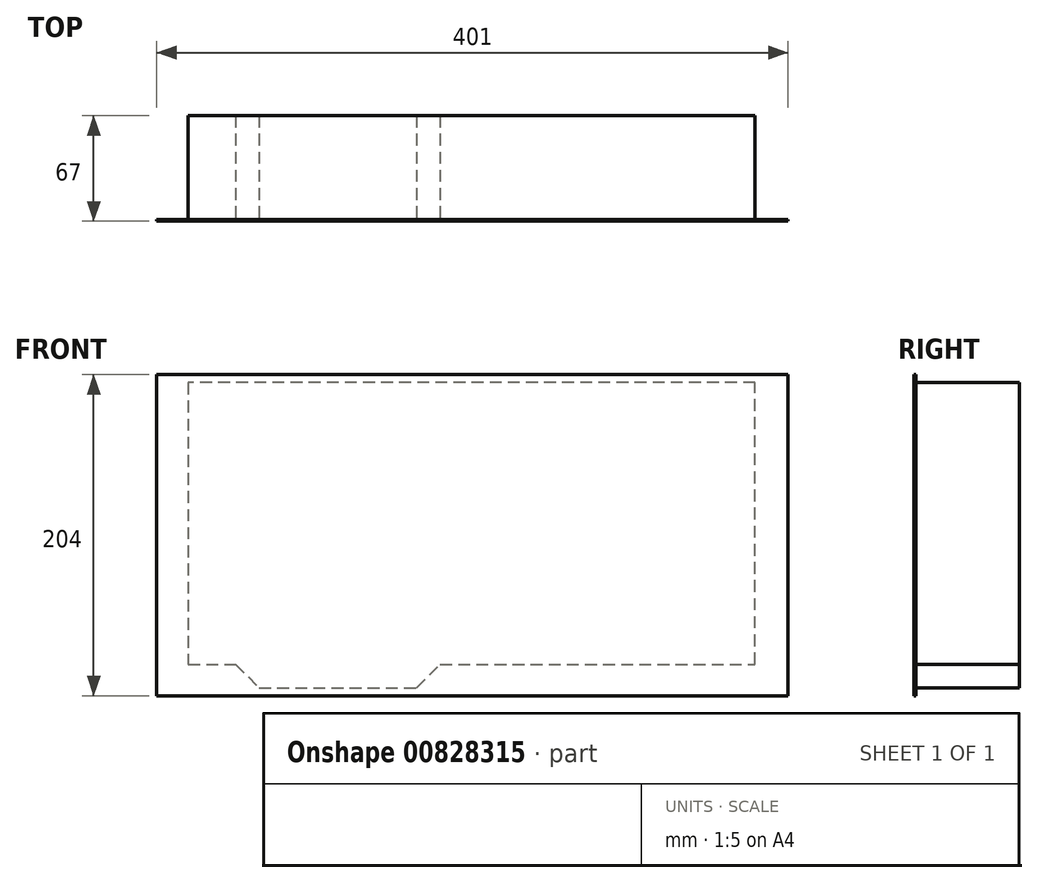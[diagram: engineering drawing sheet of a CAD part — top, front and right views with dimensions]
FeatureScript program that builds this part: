
annotation { "Feature Type Name" : "Feature", "Feature Type Description" : "" }
export const myFeature = defineFeature(function(context is Context, id is Id, definition is map)
    precondition{}
    {
        {
            var Q0;
            Q0=qCreatedBy(makeId("Front.planeOp"),FACE);
            var sketch = newSketch(context, id + "F0", { "sketchPlane" : qUnion([Q0])});
            skLineSegment(sketch, "E0.bottom", {"start": v(0, 0) * mm, "end": v(401, 0) * mm});
            skLineSegment(sketch, "E0.top", {"start": v(0, 204) * mm, "end": v(401, 204) * mm});
            skLineSegment(sketch, "E0.left", {"start": v(0, 0) * mm, "end": v(0, 204) * mm});
            skLineSegment(sketch, "E0.right", {"start": v(401, 0) * mm, "end": v(401, 204) * mm});
            skSolve(sketch);
        }
        {
            var Q0;
            Q0=makeQuery(id+"F0.imprint","IMPRINT",FACE,{"disambiguationData":[TD([[makeQuery(id+"F0.imprint","IMPRINT",EDGE,{"derivedFrom":sQuery(id+"F0.wireOp",EDGE,"E0.bottom")}),1.0]])]});
            extrude(context, id + "F1", {"entities" : qUnion([Q0]), "depth" : 1 * mm, "offsetDistance" : 25 * mm});
        }
        {
            var Q0;
            Q0=makeQuery(id+"F1.opExtrude","CAP_FACE",FACE,{"disambiguationData":[OSD([sQuery(id+"F0.wireOp",EDGE,"E0.bottom"),sQuery(id+"F0.wireOp",EDGE,"E0.top"),sQuery(id+"F0.wireOp",EDGE,"E0.left"),sQuery(id+"F0.wireOp",EDGE,"E0.right")])],"isStart":true});
            var sketch = newSketch(context, id + "F2", { "sketchPlane" : qUnion([Q0])});
            skLineSegment(sketch, "E1", {"start": v(-20, 199) * mm, "end": v(-20, 20) * mm});
            skLineSegment(sketch, "E2", {"start": v(-20, 20) * mm, "end": v(-50, 20) * mm});
            skLineSegment(sketch, "E3", {"start": v(-50, 20) * mm, "end": v(-65, 5) * mm});
            skLineSegment(sketch, "E4", {"start": v(-65, 5) * mm, "end": v(-165, 5) * mm});
            skLineSegment(sketch, "E5", {"start": v(-165, 5) * mm, "end": v(-180, 20) * mm});
            skLineSegment(sketch, "E6", {"start": v(-180, 20) * mm, "end": v(-380, 20) * mm});
            skLineSegment(sketch, "E7", {"start": v(-380, 20) * mm, "end": v(-380, 199) * mm});
            skLineSegment(sketch, "E8", {"start": v(-380, 199) * mm, "end": v(-20, 199) * mm});
            skPoint(sketch, "E9.center.orphan", {"position": v(-60, 180) * mm});
            skSolve(sketch);
        }
        {
            var Q0;
            Q0=makeQuery(id+"F2.imprint","IMPRINT",FACE,{"disambiguationData":[TD([[makeQuery(id+"F2.imprint","IMPRINT",EDGE,{"derivedFrom":sQuery(id+"F2.wireOp",EDGE,"E1")}),-1.0]])]});
            extrude(context, id + "F3", {"entities" : qUnion([Q0]), "operationType" : NewBodyOperationType.ADD, "depth" : 66 * mm, "offsetDistance" : 25 * mm});
        }
    });
